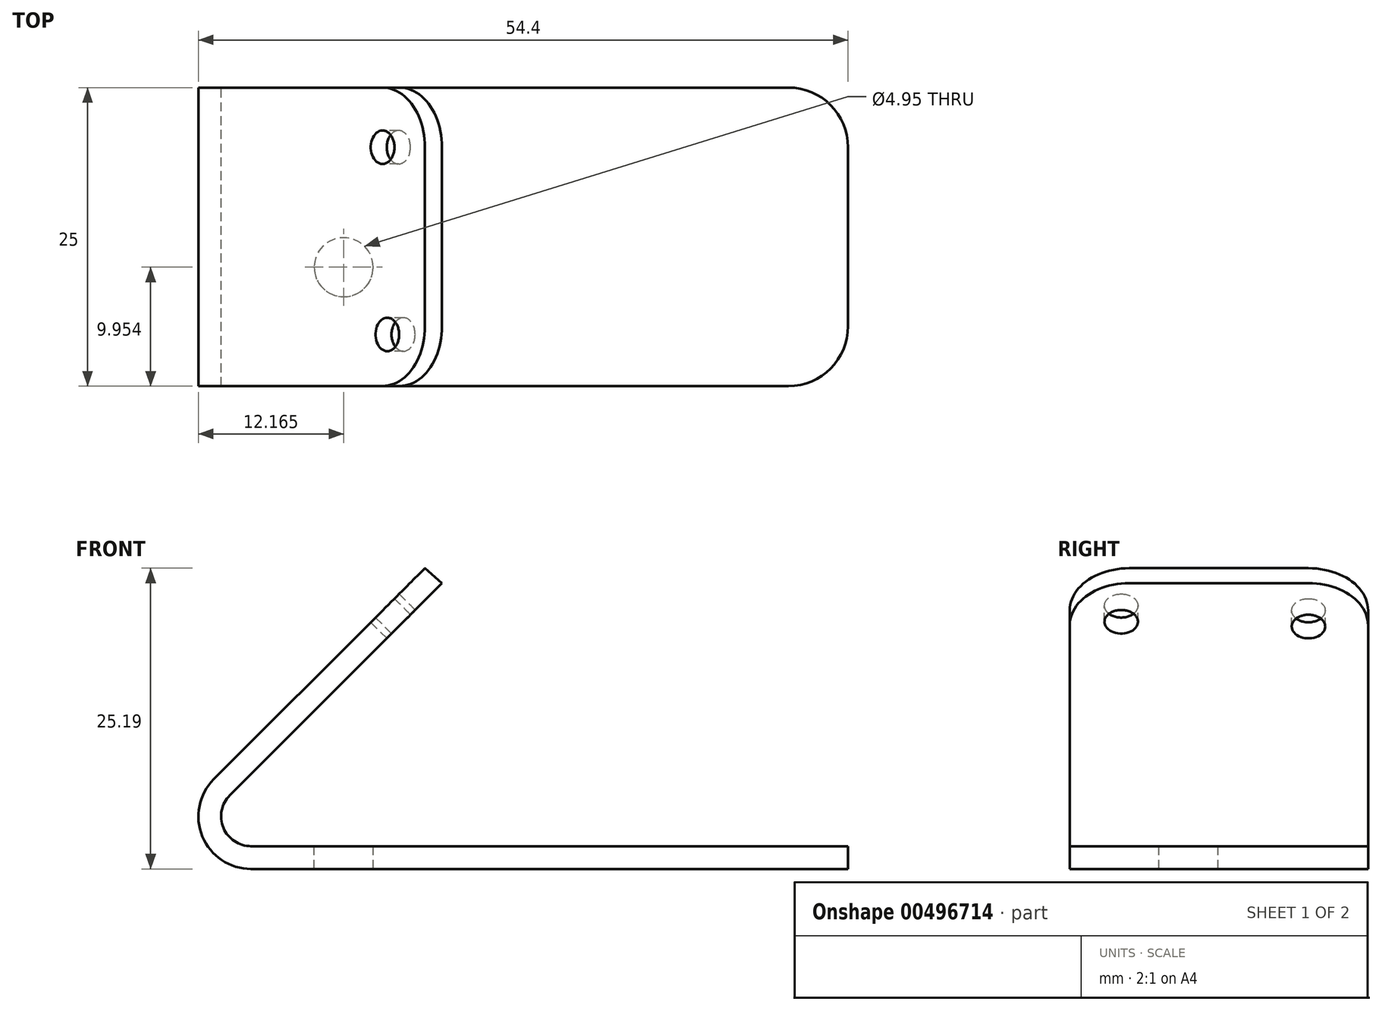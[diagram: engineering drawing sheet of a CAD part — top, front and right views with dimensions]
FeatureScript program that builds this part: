
annotation { "Feature Type Name" : "Feature", "Feature Type Description" : "" }
export const myFeature = defineFeature(function(context is Context, id is Id, definition is map)
    precondition{}
    {
        {
            var Q0;
            Q0=qCreatedBy(makeId("Front.planeOp"),FACE);
            var sketch = newSketch(context, id + "F0", { "sketchPlane" : qUnion([Q0])});
            skLineSegment(sketch, "E0", {"start": v(0, 0) * mm, "end": v(-50, 0) * mm});
            skLineSegment(sketch, "E1", {"start": v(-53.11, 7.51) * mm, "end": v(-35.43, 25.19) * mm});
            skPoint(sketch, "E2.visualSharp", {"position": v(-60.62, 0) * mm});
            skArc(sketch, "E2.filletArc", {"start": v(-53.11, 7.51) * mm, "mid": v(-54.07, 2.72) * mm, "end": v(-50, 0) * mm});
            skLineSegment(sketch, "E3.0", {"start": v(-51.77, 6.17) * mm, "end": v(-34, 23.94) * mm});
            skArc(sketch, "E3.1", {"start": v(-51.77, 6.17) * mm, "mid": v(-52.3, 3.44) * mm, "end": v(-50, 1.9) * mm});
            skLineSegment(sketch, "E3.2", {"start": v(0, 1.9) * mm, "end": v(-50, 1.9) * mm});
            skLineSegment(sketch, "E4", {"start": v(-34, 23.94) * mm, "end": v(-35.43, 25.19) * mm});
            skLineSegment(sketch, "E5", {"start": v(0, 1.9) * mm, "end": v(0, 0) * mm});
            skSolve(sketch);
        }
        {
            var Q0;
            Q0=qCreatedBy(makeId("Front.planeOp"),FACE);
            var sketch = newSketch(context, id + "F1", { "sketchPlane" : qUnion([Q0])});
            skSolve(sketch);
        }
        {
            var Q0;
            Q0 = qSketchRegion(id + "F1", true);
            var Q1;
            Q1=makeQuery(id+"F0.imprint","IMPRINT",FACE,{"disambiguationData":[TD([[makeQuery(id+"F0.imprint","IMPRINT",EDGE,{"derivedFrom":sQuery(id+"F0.wireOp",EDGE,"E0")}),-1.0]])]});
            extrude(context, id + "F2", {"entities" : qUnion([Q0, Q1]), "depth" : 25 * mm});
        }
        {
            var Q0;
            Q0=makeQuery(id+"F2.opExtrude","CAP_EDGE",EDGE,{"disambiguationData":[OSD([sQuery(id+"F0.wireOp",EDGE,"E4")])],"isStart":false});
            var Q1;
            Q1=makeQuery(id+"F2.opExtrude","CAP_EDGE",EDGE,{"disambiguationData":[OSD([sQuery(id+"F0.wireOp",EDGE,"E4")])],"isStart":true});
            var Q2;
            Q2=makeQuery(id+"F2.opExtrude","CAP_EDGE",EDGE,{"disambiguationData":[OSD([sQuery(id+"F0.wireOp",EDGE,"E5")])],"isStart":false});
            var Q3;
            Q3=makeQuery(id+"F2.opExtrude","CAP_EDGE",EDGE,{"disambiguationData":[OSD([sQuery(id+"F0.wireOp",EDGE,"E5")])],"isStart":true});
            fillet(context, id + "F3", {"entities" : qUnion([Q0, Q1, Q2, Q3]), "radius" : 5 * mm, "tangentPropagation" : true, "allowEdgeOverflow" : false});
        }
        {
            var Q0;
            Q0=makeQuery(id+"F2.opExtrude","SWEPT_FACE",FACE,{"disambiguationData":[OSD([sQuery(id+"F0.wireOp",EDGE,"E1")])]});
            var sketch = newSketch(context, id + "F4", { "sketchPlane" : qUnion([Q0])});
            skCircle(sketch, "E6", {"center": v(20.68, -11.7) * mm, "radius": 1.4 * mm});
            skCircle(sketch, "E7", {"center": v(5, -12.26) * mm, "radius": 1.4 * mm});
            skSolve(sketch);
        }
        {
            var Q0;
            Q0=makeQuery(id+"F4.imprint","IMPRINT",FACE,{"disambiguationData":[TD([[makeQuery(id+"F4.imprint","IMPRINT",EDGE,{"derivedFrom":sQuery(id+"F4.wireOp",EDGE,"E7")}),1.0]])]});
            var Q1;
            Q1=makeQuery(id+"F4.imprint","IMPRINT",FACE,{"disambiguationData":[TD([[makeQuery(id+"F4.imprint","IMPRINT",EDGE,{"derivedFrom":sQuery(id+"F4.wireOp",EDGE,"E6")}),1.0]])]});
            extrude(context, id + "F5", {"entities" : qUnion([Q0, Q1]), "operationType" : NewBodyOperationType.REMOVE, "endBound" : BoundingType.SYMMETRIC, "oppositeDirection" : true, "depth" : 25 * mm});
        }
        {
            var Q0;
            Q0=makeQuery(id+"F2.opExtrude","SWEPT_FACE",FACE,{"disambiguationData":[OSD([sQuery(id+"F0.wireOp",EDGE,"E3.2")])]});
            var sketch = newSketch(context, id + "F6", { "sketchPlane" : qUnion([Q0])});
            skCircle(sketch, "E8", {"center": v(-42.24, -15.05) * mm, "radius": 2.47 * mm});
            skSolve(sketch);
        }
        {
            var Q0;
            Q0=makeQuery(id+"F6.imprint","IMPRINT",FACE,{"disambiguationData":[TD([[makeQuery(id+"F6.imprint","IMPRINT",EDGE,{"derivedFrom":sQuery(id+"F6.wireOp",EDGE,"E8")}),1.0]])]});
            var Q1;
            Q1=sQuery(id+"F6.wireOp",EDGE,"E8");
            extrude(context, id + "F7", {"entities" : qUnion([Q0]), "operationType" : NewBodyOperationType.REMOVE, "surfaceEntities" : qUnion([Q1]), "endBound" : BoundingType.THROUGH_ALL, "oppositeDirection" : true, "depth" : 25 * mm});
        }
    });
